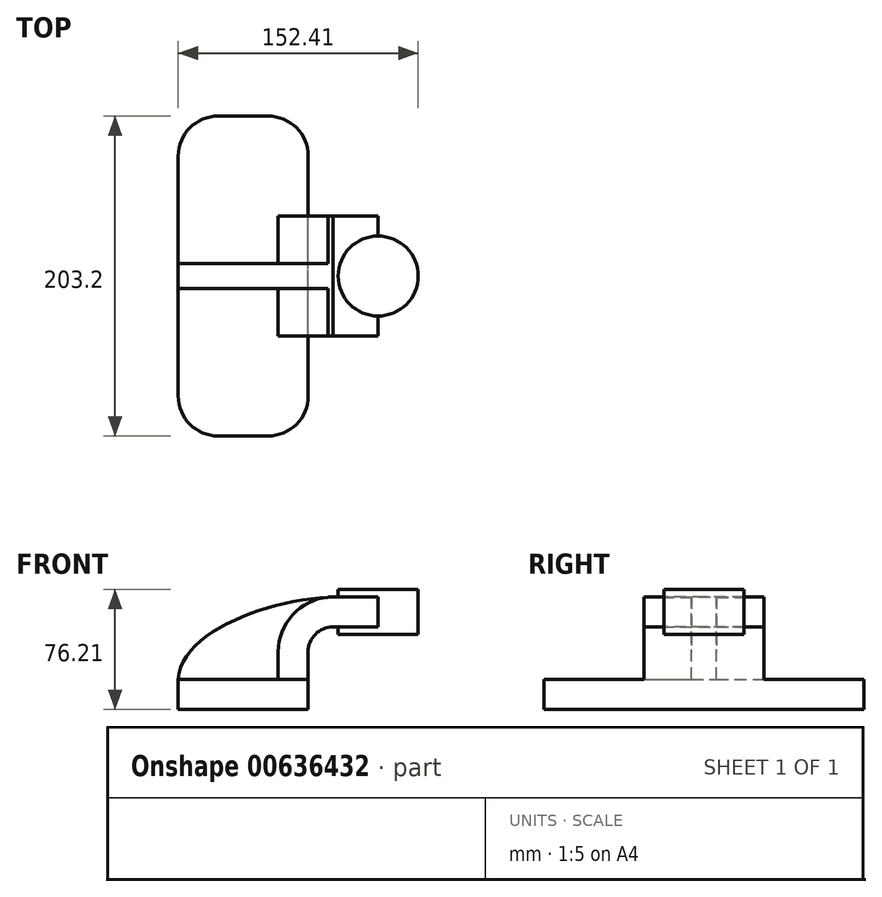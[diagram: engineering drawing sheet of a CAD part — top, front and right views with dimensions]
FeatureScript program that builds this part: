
annotation { "Feature Type Name" : "Feature", "Feature Type Description" : "" }
export const myFeature = defineFeature(function(context is Context, id is Id, definition is map)
    precondition{}
    {
        {
            var Q0;
            Q0=qCreatedBy(makeId("Front.planeOp"),FACE);
            var sketch = newSketch(context, id + "F0", { "sketchPlane" : qUnion([Q0])});
            skLineSegment(sketch, "E0.rect.bottom", {"start": v(-41.28, 9.53) * mm, "end": v(41.27, 9.53) * mm});
            skLineSegment(sketch, "E0.rect.top", {"start": v(-41.27, -9.53) * mm, "end": v(41.28, -9.53) * mm});
            skLineSegment(sketch, "E0.rect.left", {"start": v(-41.28, 9.53) * mm, "end": v(-41.27, -9.53) * mm});
            skLineSegment(sketch, "E0.rect.right", {"start": v(41.27, 9.53) * mm, "end": v(41.28, -9.53) * mm});
            skPoint(sketch, "E0.rect.middle", {"position": v(0, 0) * mm});
            skLineSegment(sketch, "E1", {"start": v(41.27, 9.53) * mm, "end": v(41.27, 27) * mm});
            skArc(sketch, "E2", {"start": v(41.27, 27) * mm, "mid": v(45.92, 38.23) * mm, "end": v(57.15, 42.88) * mm});
            skLineSegment(sketch, "E3", {"start": v(57.15, 42.88) * mm, "end": v(85.72, 42.88) * mm});
            skLineSegment(sketch, "E4.rect.bottom", {"start": v(60.32, 38.1) * mm, "end": v(111.12, 38.1) * mm});
            skLineSegment(sketch, "E4.rect.top", {"start": v(60.32, 66.67) * mm, "end": v(111.12, 66.67) * mm});
            skLineSegment(sketch, "E4.rect.left", {"start": v(60.32, 38.1) * mm, "end": v(60.32, 66.67) * mm});
            skLineSegment(sketch, "E4.rect.right", {"start": v(111.12, 38.1) * mm, "end": v(111.12, 66.67) * mm});
            skPoint(sketch, "E4.rect.middle", {"position": v(85.72, 52.39) * mm});
            skLineSegment(sketch, "E5.0", {"start": v(57.15, 61.93) * mm, "end": v(85.72, 61.93) * mm});
            skArc(sketch, "E5.1", {"start": v(22.23, 27) * mm, "mid": v(32.45, 51.7) * mm, "end": v(57.15, 61.93) * mm});
            skLineSegment(sketch, "E5.2", {"start": v(22.22, 9.52) * mm, "end": v(22.22, 27) * mm});
            skLineSegment(sketch, "E6", {"start": v(85.72, 38.1) * mm, "end": v(85.72, 66.67) * mm});
            skFitSpline(sketch, "E7", {"points": [v(-41.28, 9.53) * mm, v(57.15, 61.93) * mm], "startDerivative": vector(5.2, 92.34) * mm, "endDerivative": vector(120.92, 4.22) * mm});
            skSolve(sketch);
        }
        {
            var Q0;
            Q0=makeQuery(id+"F0.imprint","IMPRINT",FACE,{"disambiguationData":[TD([[makeQuery(id+"F0.imprint","IMPRINT",EDGE,{"derivedFrom":sQuery(id+"F0.wireOp",EDGE,"E0.rect.top")}),1.0]])]});
            extrude(context, id + "F1", {"entities" : qUnion([Q0]), "flatOperationType" : FlatOperationType.REMOVE, "offsetDistance" : 25 * mm, "depth" : 203.2 * mm, "domain" : OperationDomain.MODEL, "symmetric" : true});
        }
        {
            var Q0;
            {var subQ9=sQuery(id+"F0.wireOp",EDGE,"E1");Q0=makeQuery(id+"F0.imprint","IMPRINT",FACE,{"disambiguationData":[TD([[makeQuery(id+"F0.imprint","IMPRINT",EDGE,{"derivedFrom":subQ9}),1.0]])]});}
            var Q1;
            {var subQ0=sQuery(id+"F0.wireOp",EDGE,"E6");var subQ1=sQuery(id+"F0.wireOp",EDGE,"E3");var subQ2=makeQuery(id+"F0.imprint","INTERSECT",VERTEX,{"derivedFrom":[subQ1,subQ0]});Q1=makeQuery(id+"F0.imprint","IMPRINT",FACE,{"disambiguationData":[TD([[makeQuery(id+"F0.imprint","IMPRINT",EDGE,{"disambiguationData":[TD([[subQ2,1.0]])],"derivedFrom":subQ1}),1.0]])]});}
            extrude(context, id + "F2", {"entities" : qUnion([Q0, Q1]), "operationType" : NewBodyOperationType.ADD, "flatOperationType" : FlatOperationType.REMOVE, "offsetDistance" : 25.4 * mm, "depth" : 76.2 * mm, "domain" : OperationDomain.MODEL, "symmetric" : true});
        }
        {
            var Q0;
            {var subQ3=sQuery(id+"F0.wireOp",EDGE,"E5.2");Q0=makeQuery(id+"F0.imprint","IMPRINT",FACE,{"disambiguationData":[TD([[makeQuery(id+"F0.imprint","IMPRINT",EDGE,{"derivedFrom":subQ3}),1.0]])]});}
            extrude(context, id + "F3", {"entities" : qUnion([Q0]), "operationType" : NewBodyOperationType.ADD, "flatOperationType" : FlatOperationType.REMOVE, "offsetDistance" : 25.4 * mm, "depth" : 15.88 * mm, "domain" : OperationDomain.MODEL, "symmetric" : true});
        }
        {
            var Q0;
            {var subQ5=sQuery(id+"F0.wireOp",EDGE,"E4.rect.right");Q0=makeQuery(id+"F0.imprint","IMPRINT",FACE,{"disambiguationData":[TD([[makeQuery(id+"F0.imprint","IMPRINT",EDGE,{"derivedFrom":subQ5}),1.0]])]});}
            var Q1;
            Q1=sQuery(id+"F0.wireOp",EDGE,"E6");
            revolve(context, id + "F4", {"operationType" : NewBodyOperationType.ADD, "entities" : qUnion([Q0]), "axis" : qUnion([Q1]), "revolveType" : RevolveType.FULL});
        }
        {
            var Q0;
            Q0=makeQuery(id+"F1.opExtrude","CAP_EDGE",EDGE,{"disambiguationData":[OSD([sQuery(id+"F0.wireOp",EDGE,"E0.rect.right")])],"isStart":false});
            var Q1;
            Q1=makeQuery(id+"F1.opExtrude","CAP_EDGE",EDGE,{"disambiguationData":[OSD([sQuery(id+"F0.wireOp",EDGE,"E0.rect.left")])],"isStart":false});
            var Q2;
            Q2=makeQuery(id+"F1.opExtrude","CAP_EDGE",EDGE,{"disambiguationData":[OSD([sQuery(id+"F0.wireOp",EDGE,"E0.rect.right")])],"isStart":true});
            var Q3;
            Q3=makeQuery(id+"F1.opExtrude","CAP_EDGE",EDGE,{"disambiguationData":[OSD([sQuery(id+"F0.wireOp",EDGE,"E0.rect.left")])],"isStart":true});
            fillet(context, id + "F5", {"entities" : qUnion([Q0, Q1, Q2, Q3]), "radius" : 25.4 * mm, "tangentPropagation" : true, "allowEdgeOverflow" : false});
        }
    });
